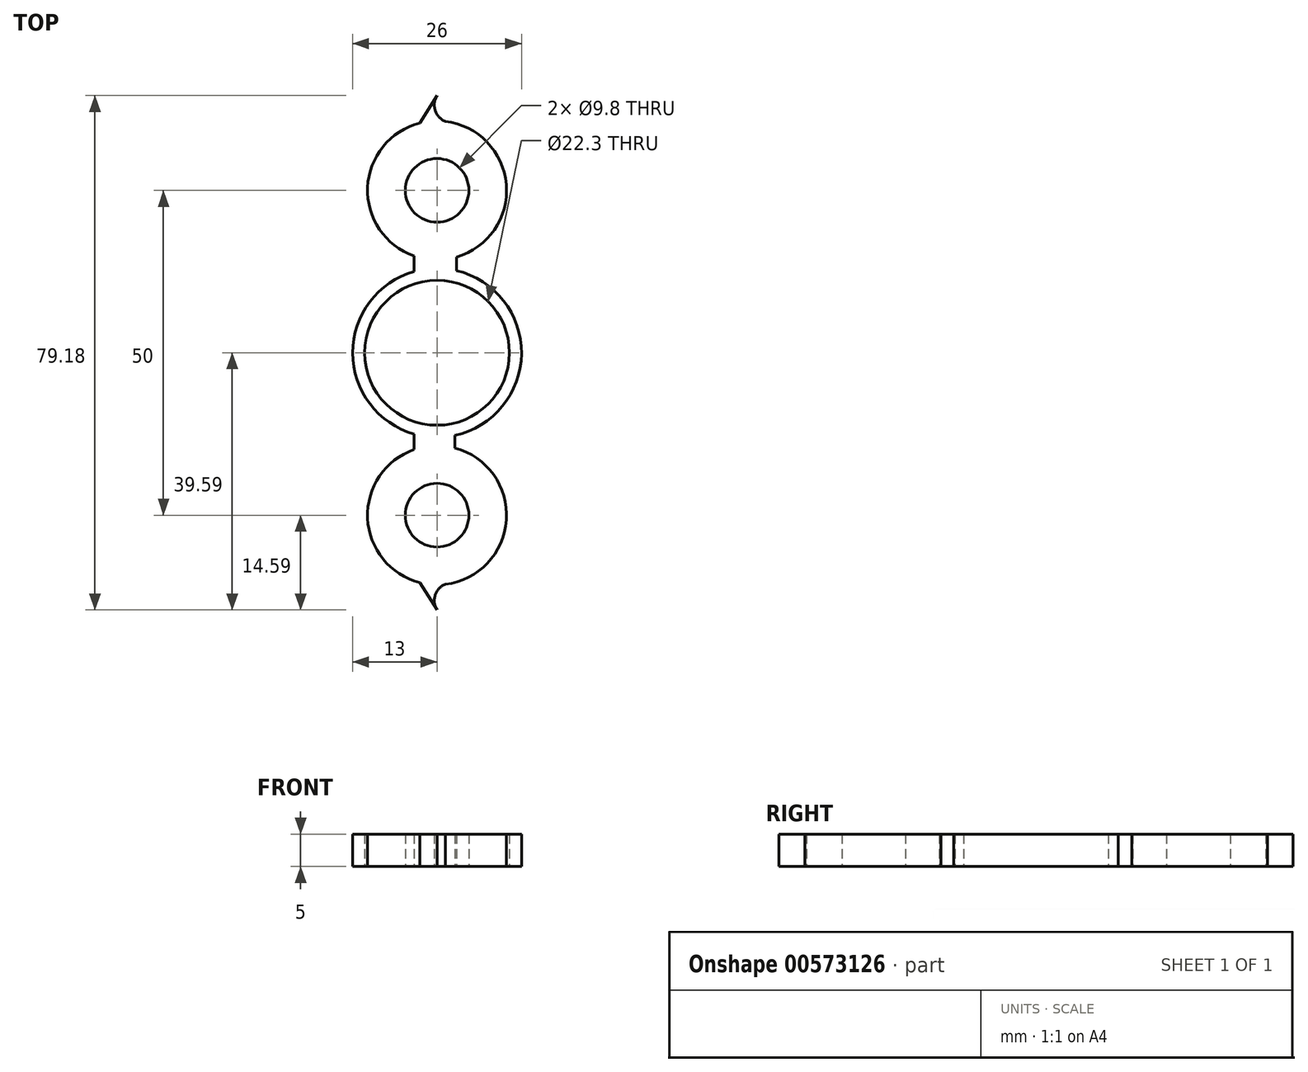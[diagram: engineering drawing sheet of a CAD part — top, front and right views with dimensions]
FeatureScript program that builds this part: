
annotation { "Feature Type Name" : "Feature", "Feature Type Description" : "" }
export const myFeature = defineFeature(function(context is Context, id is Id, definition is map)
    precondition{}
    {
        {
            var Q0;
            Q0=qCreatedBy(makeId("Top.planeOp"),FACE);
            var sketch = newSketch(context, id + "F0", { "sketchPlane" : qUnion([Q0])});
            skCircle(sketch, "E0", {"center": v(0, 0) * mm, "radius": 13 * mm});
            skCircle(sketch, "E1", {"center": v(0, 25) * mm, "radius": 4.9 * mm});
            skCircle(sketch, "E2.MirrorC", {"center": v(0, -25) * mm, "radius": 4.9 * mm});
            skLineSegment(sketch, "E3.bottom", {"start": v(0, 4.7) * mm, "end": v(-3.47, 4.7) * mm});
            skLineSegment(sketch, "E3.top", {"start": v(3.24, 27.2) * mm, "end": v(-3.64, 27.2) * mm});
            skLineSegment(sketch, "E4.MirrorCS", {"start": v(-3.47, -4.7) * mm, "end": v(-3.64, -27.2) * mm});
            skLineSegment(sketch, "E5.MirrorCS", {"start": v(2.65, -4.7) * mm, "end": v(2.83, -27.54) * mm});
            skLineSegment(sketch, "E6", {"start": v(-3.64, -27.2) * mm, "end": v(2.83, -27.54) * mm});
            skLineSegment(sketch, "E7", {"start": v(0, 4.7) * mm, "end": v(2.83, 4.7) * mm});
            skLineSegment(sketch, "E8", {"start": v(3.24, 27.2) * mm, "end": v(2.83, 4.7) * mm});
            skLineSegment(sketch, "E9", {"start": v(-3.64, 27.2) * mm, "end": v(-3.47, 4.7) * mm});
            skLineSegment(sketch, "E10", {"start": v(-3.47, -4.7) * mm, "end": v(2.65, -4.7) * mm});
            skCircle(sketch, "E11", {"center": v(0, 25) * mm, "radius": 10.7 * mm});
            skCircle(sketch, "E12.MirrorC", {"center": v(0, -25) * mm, "radius": 10.7 * mm});
            skLineSegment(sketch, "E13", {"start": v(-2.67, 35.37) * mm, "end": v(0, 39.59) * mm});
            skArc(sketch, "E14", {"start": v(0, 39.59) * mm, "mid": v(-0.05, 36.78) * mm, "end": v(2.4, 35.43) * mm});
            skArc(sketch, "E15.MirrorCS", {"start": v(0, -39.59) * mm, "mid": v(-0.05, -36.78) * mm, "end": v(2.4, -35.43) * mm});
            skLineSegment(sketch, "E16.MirrorCS", {"start": v(-2.67, -35.37) * mm, "end": v(0, -39.59) * mm});
            skCircle(sketch, "E17", {"center": v(0, 0) * mm, "radius": 11.15 * mm});
            skSolve(sketch);
        }
        {
            var Q0;
            Q0 = qSketchRegion(id + "F0", true);
            extrude(context, id + "F1", {"entities" : qUnion([Q0]), "depth" : 5 * mm, "offsetDistance" : 25.4 * mm});
        }
    });
